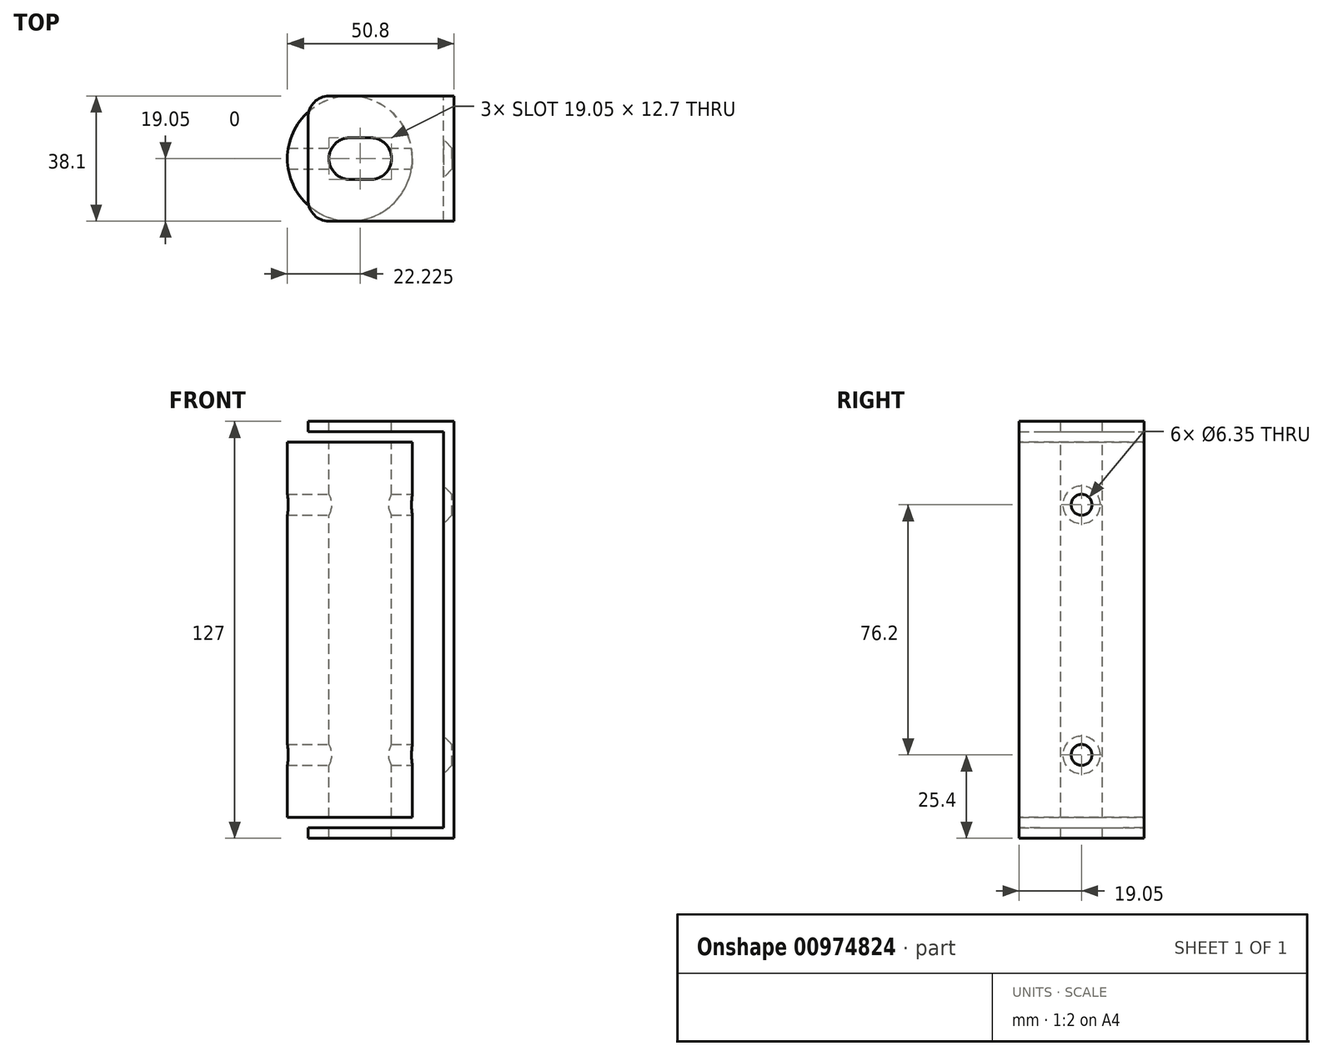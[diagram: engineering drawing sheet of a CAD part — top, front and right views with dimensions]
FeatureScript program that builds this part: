
annotation { "Feature Type Name" : "Feature", "Feature Type Description" : "" }
export const myFeature = defineFeature(function(context is Context, id is Id, definition is map)
    precondition{}
    {
        {
            var Q0;
            Q0=qCreatedBy(makeId("Top.planeOp"),FACE);
            var sketch = newSketch(context, id + "F0", { "sketchPlane" : qUnion([Q0])});
            skCircle(sketch, "E0", {"center": v(12.7, 0) * mm, "radius": 19.05 * mm});
            skCircle(sketch, "E1", {"center": v(12.7, 0) * mm, "radius": 6.35 * mm});
            skSolve(sketch);
        }
        {
            var Q0;
            Q0 = qSketchRegion(id + "F0", true);
            extrude(context, id + "F1", {"entities" : qUnion([Q0]), "oppositeDirection" : true, "depth" : 120.65 * mm, "offsetDistance" : 25.4 * mm, "hasSecondDirection" : true, "secondDirectionOppositeDirection" : true, "secondDirectionDepth" : 6.35 * mm});
        }
        {
            var Q0;
            Q0=qCreatedBy(makeId("Front.planeOp"),FACE);
            var sketch = newSketch(context, id + "F2", { "sketchPlane" : qUnion([Q0])});
            skLineSegment(sketch, "E2", {"start": v(0, 0) * mm, "end": v(44.45, 0) * mm});
            skLineSegment(sketch, "E3", {"start": v(44.45, 0) * mm, "end": v(44.45, -127) * mm});
            skLineSegment(sketch, "E4", {"start": v(44.45, -127) * mm, "end": v(0, -127) * mm});
            skLineSegment(sketch, "E5", {"start": v(0, -127) * mm, "end": v(0, -123.83) * mm});
            skLineSegment(sketch, "E6", {"start": v(0, -123.83) * mm, "end": v(41.28, -123.83) * mm});
            skLineSegment(sketch, "E7", {"start": v(41.28, -123.83) * mm, "end": v(41.28, -3.17) * mm});
            skLineSegment(sketch, "E8", {"start": v(41.28, -3.18) * mm, "end": v(0, -3.18) * mm});
            skLineSegment(sketch, "E9", {"start": v(0, -3.18) * mm, "end": v(0, 0) * mm});
            skSolve(sketch);
        }
        {
            var Q0;
            Q0 = qSketchRegion(id + "F2", true);
            extrude(context, id + "F3", {"entities" : qUnion([Q0]), "endBound" : BoundingType.SYMMETRIC, "depth" : 38.1 * mm, "offsetDistance" : 25.4 * mm});
        }
        {
            var Q0;
            Q0=makeQuery(id+"F3.opExtrude","SWEPT_FACE",FACE,{"disambiguationData":[OSD([sQuery(id+"F2.wireOp",EDGE,"E2")])]});
            var sketch = newSketch(context, id + "F4", { "sketchPlane" : qUnion([Q0])});
            skCircle(sketch, "E10", {"center": v(12.7, 0) * mm, "radius": 6.35 * mm});
            skCircle(sketch, "E11", {"center": v(19.05, 0) * mm, "radius": 6.35 * mm});
            skLineSegment(sketch, "E12", {"start": v(12.7, 6.35) * mm, "end": v(19.05, 6.35) * mm});
            skLineSegment(sketch, "E13", {"start": v(19.05, -6.35) * mm, "end": v(12.7, -6.35) * mm});
            skSolve(sketch);
        }
        {
            var Q0;
            {var subQ0=sQuery(id+"F4.wireOp",EDGE,"E11");var subQ1=sQuery(id+"F4.wireOp",EDGE,"E10");var subQ6=makeQuery(id+"F4.imprint","INTERSECT",VERTEX,{"disambiguationData":[OD(0.0)],"derivedFrom":[subQ1,subQ0]});Q0=makeQuery(id+"F4.imprint","IMPRINT",FACE,{"disambiguationData":[TD([[makeQuery(id+"F4.imprint","IMPRINT",EDGE,{"disambiguationData":[TD([[subQ6,1.0]])],"derivedFrom":subQ1}),-1.0]])]});}
            var Q1;
            {var subQ0=sQuery(id+"F4.wireOp",EDGE,"E10");var subQ1=makeQuery(id+"F4.imprint","INTERSECT",VERTEX,{"derivedFrom":[subQ0,sQuery(id+"F4.wireOp",EDGE,"E12")]});Q1=makeQuery(id+"F4.imprint","IMPRINT",FACE,{"disambiguationData":[TD([[makeQuery(id+"F4.imprint","IMPRINT",EDGE,{"disambiguationData":[TD([[subQ1,1.0]])],"derivedFrom":subQ0}),1.0]])]});}
            var Q2;
            {var subQ0=sQuery(id+"F4.wireOp",EDGE,"E11");var subQ1=sQuery(id+"F4.wireOp",EDGE,"E10");var subQ2=makeQuery(id+"F4.imprint","INTERSECT",VERTEX,{"disambiguationData":[OD(0.0)],"derivedFrom":[subQ1,subQ0]});Q2=makeQuery(id+"F4.imprint","IMPRINT",FACE,{"disambiguationData":[TD([[makeQuery(id+"F4.imprint","IMPRINT",EDGE,{"disambiguationData":[TD([[subQ2,1.0]])],"derivedFrom":subQ1}),1.0]])]});}
            var Q3;
            {var subQ0=sQuery(id+"F4.wireOp",EDGE,"E12");Q3=makeQuery(id+"F4.imprint","IMPRINT",FACE,{"disambiguationData":[TD([[makeQuery(id+"F4.imprint","IMPRINT",EDGE,{"derivedFrom":subQ0}),-1.0]])]});}
            var Q4;
            {var subQ0=sQuery(id+"F4.wireOp",EDGE,"E13");var subQ1=sQuery(id+"F4.wireOp",EDGE,"E10");var subQ2=makeQuery(id+"F4.imprint","INTERSECT",VERTEX,{"derivedFrom":[subQ1,subQ0]});Q4=makeQuery(id+"F4.imprint","IMPRINT",FACE,{"disambiguationData":[TD([[makeQuery(id+"F4.imprint","IMPRINT",EDGE,{"disambiguationData":[TD([[subQ2,-1.0]])],"derivedFrom":subQ1}),-1.0]])]});}
            extrude(context, id + "F5", {"entities" : qUnion([Q0, Q1, Q2, Q3, Q4]), "operationType" : NewBodyOperationType.REMOVE, "endBound" : BoundingType.THROUGH_ALL, "oppositeDirection" : true, "depth" : 25.4 * mm, "offsetDistance" : 25.4 * mm});
        }
        {
            var Q0;
            Q0=makeQuery(id+"F3.opExtrude","CAP_EDGE",EDGE,{"disambiguationData":[OSD([sQuery(id+"F2.wireOp",EDGE,"E9")])],"isStart":true});
            var Q1;
            Q1=makeQuery(id+"F3.opExtrude","CAP_EDGE",EDGE,{"disambiguationData":[OSD([sQuery(id+"F2.wireOp",EDGE,"E9")])],"isStart":false});
            var Q2;
            Q2=makeQuery(id+"F3.opExtrude","CAP_EDGE",EDGE,{"disambiguationData":[OSD([sQuery(id+"F2.wireOp",EDGE,"E5")])],"isStart":false});
            var Q3;
            Q3=makeQuery(id+"F3.opExtrude","CAP_EDGE",EDGE,{"disambiguationData":[OSD([sQuery(id+"F2.wireOp",EDGE,"E5")])],"isStart":true});
            fillet(context, id + "F6", {"entities" : qUnion([Q0, Q1, Q2, Q3]), "tangentPropagation" : true, "radius" : 6.35 * mm, "defaultsChanged" : true, "vertexSettings" : [], "allowEdgeOverflow" : false});
        }
        {
            var Q0;
            Q0=makeQuery(id+"F3.opExtrude","SWEPT_FACE",FACE,{"disambiguationData":[OSD([sQuery(id+"F2.wireOp",EDGE,"E3")])]});
            var sketch = newSketch(context, id + "F7", { "sketchPlane" : qUnion([Q0])});
            skCircle(sketch, "E14", {"center": v(0, -25.4) * mm, "radius": 3.18 * mm});
            skCircle(sketch, "E15", {"center": v(0, -101.6) * mm, "radius": 3.18 * mm});
            skSolve(sketch);
        }
        {
            var Q0;
            Q0 = qSketchRegion(id + "F7", true);
            extrude(context, id + "F8", {"entities" : qUnion([Q0]), "operationType" : NewBodyOperationType.REMOVE, "endBound" : BoundingType.THROUGH_ALL, "oppositeDirection" : true, "depth" : 25.4 * mm, "offsetDistance" : 25.4 * mm});
        }
        {
            var Q0;
            Q0=makeQuery(id+"F8.boolean.opBoolean","INTERSECT",EDGE,{"derivedFrom":[makeQuery(id+"F3.opExtrude","SWEPT_FACE",FACE,{"disambiguationData":[OSD([sQuery(id+"F2.wireOp",EDGE,"E7")])]}),makeQuery(id+"F8.opExtrude","SWEPT_FACE",FACE,{"disambiguationData":[OSD([sQuery(id+"F7.wireOp",EDGE,"E14")])]})]});
            var Q1;
            Q1=makeQuery(id+"F8.boolean.opBoolean","INTERSECT",EDGE,{"derivedFrom":[makeQuery(id+"F3.opExtrude","SWEPT_FACE",FACE,{"disambiguationData":[OSD([sQuery(id+"F2.wireOp",EDGE,"E7")])]}),makeQuery(id+"F8.opExtrude","SWEPT_FACE",FACE,{"disambiguationData":[OSD([sQuery(id+"F7.wireOp",EDGE,"E15")])]})]});
            chamfer(context, id + "F9", {"entities" : qUnion([Q0, Q1]), "width" : 2.54 * mm, "tangentPropagation" : true});
        }
    });
